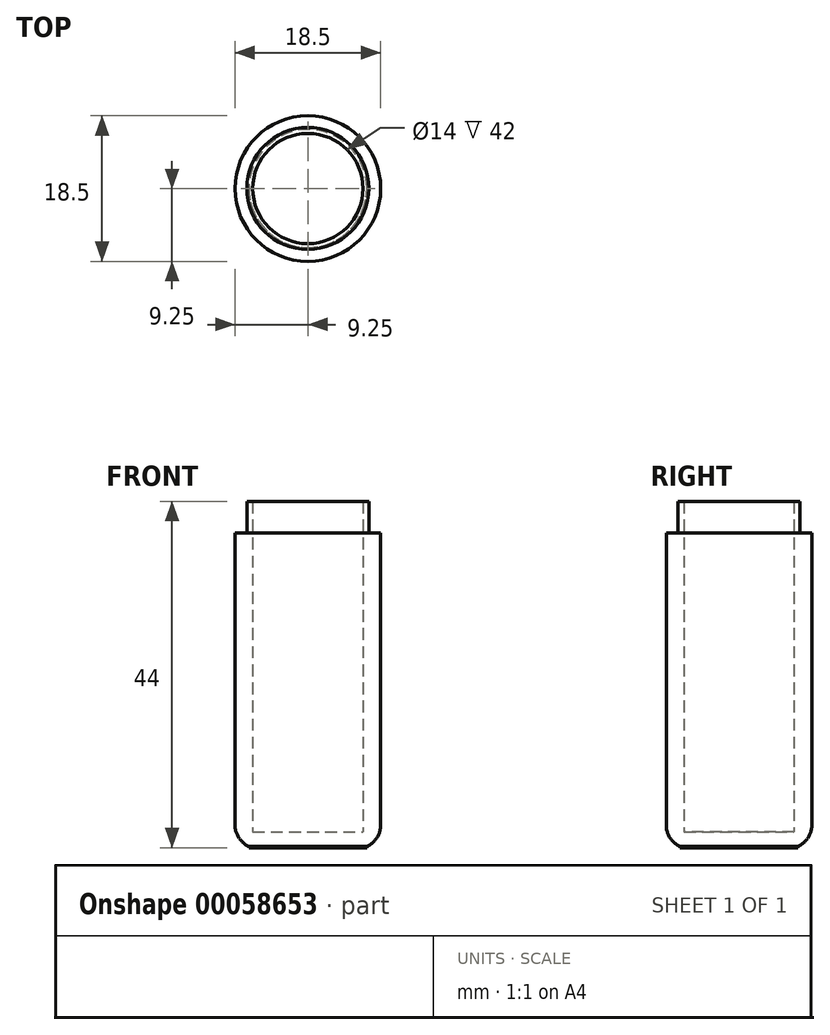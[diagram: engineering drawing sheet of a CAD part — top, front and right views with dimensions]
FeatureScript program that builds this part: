
annotation { "Feature Type Name" : "Feature", "Feature Type Description" : "" }
export const myFeature = defineFeature(function(context is Context, id is Id, definition is map)
    precondition{}
    {
        {
            var Q0;
            Q0=qCreatedBy(makeId("Top.planeOp"),FACE);
            var sketch = newSketch(context, id + "F0", { "sketchPlane" : qUnion([Q0])});
            skCircle(sketch, "E0", {"center": v(0, 0) * mm, "radius": 9.25 * mm});
            skCircle(sketch, "E1", {"center": v(0, 0) * mm, "radius": 7 * mm});
            skSolve(sketch);
        }
        {
            var Q0;
            Q0 = qSketchRegion(id + "F0", true);
            extrude(context, id + "F1", {"entities" : qUnion([Q0]), "depth" : 40 * mm});
        }
        {
            var Q0;
            Q0=makeQuery(id+"F1.opExtrude","CAP_FACE",FACE,{"disambiguationData":[OSD([sQuery(id+"F0.wireOp",EDGE,"E0"),sQuery(id+"F0.wireOp",EDGE,"E1")])],"isStart":true});
            var sketch = newSketch(context, id + "F2", { "sketchPlane" : qUnion([Q0])});
            skCircle(sketch, "E2", {"center": v(0, 0) * mm, "radius": 7.5 * mm});
            skSolve(sketch);
        }
        {
            var Q0;
            Q0=makeQuery(id+"F1.opExtrude","CAP_EDGE",EDGE,{"disambiguationData":[OSD([sQuery(id+"F0.wireOp",EDGE,"E0")])],"isStart":true});
            fillet(context, id + "F3", {"entities" : qUnion([Q0]), "radius" : 3 * mm, "tangentPropagation" : true, "allowEdgeOverflow" : false});
        }
        {
            var Q0;
            Q0 = qSketchRegion(id + "F2", true);
            extrude(context, id + "F4", {"entities" : qUnion([Q0]), "operationType" : NewBodyOperationType.ADD, "oppositeDirection" : true, "depth" : 2 * mm});
        }
        {
            var Q0;
            Q0=makeQuery(id+"F1.opExtrude","CAP_FACE",FACE,{"disambiguationData":[OSD([sQuery(id+"F0.wireOp",EDGE,"E0"),sQuery(id+"F0.wireOp",EDGE,"E1")])],"isStart":false});
            var sketch = newSketch(context, id + "F5", { "sketchPlane" : qUnion([Q0])});
            skCircle(sketch, "E3", {"center": v(0, 0) * mm, "radius": 7.75 * mm});
            skCircle(sketch, "E4.0", {"center": v(0, 0) * mm, "radius": 7 * mm});
            skSolve(sketch);
        }
        {
            var Q0;
            Q0 = qSketchRegion(id + "F5", true);
            extrude(context, id + "F6", {"entities" : qUnion([Q0]), "operationType" : NewBodyOperationType.ADD, "depth" : 4 * mm});
        }
    });
